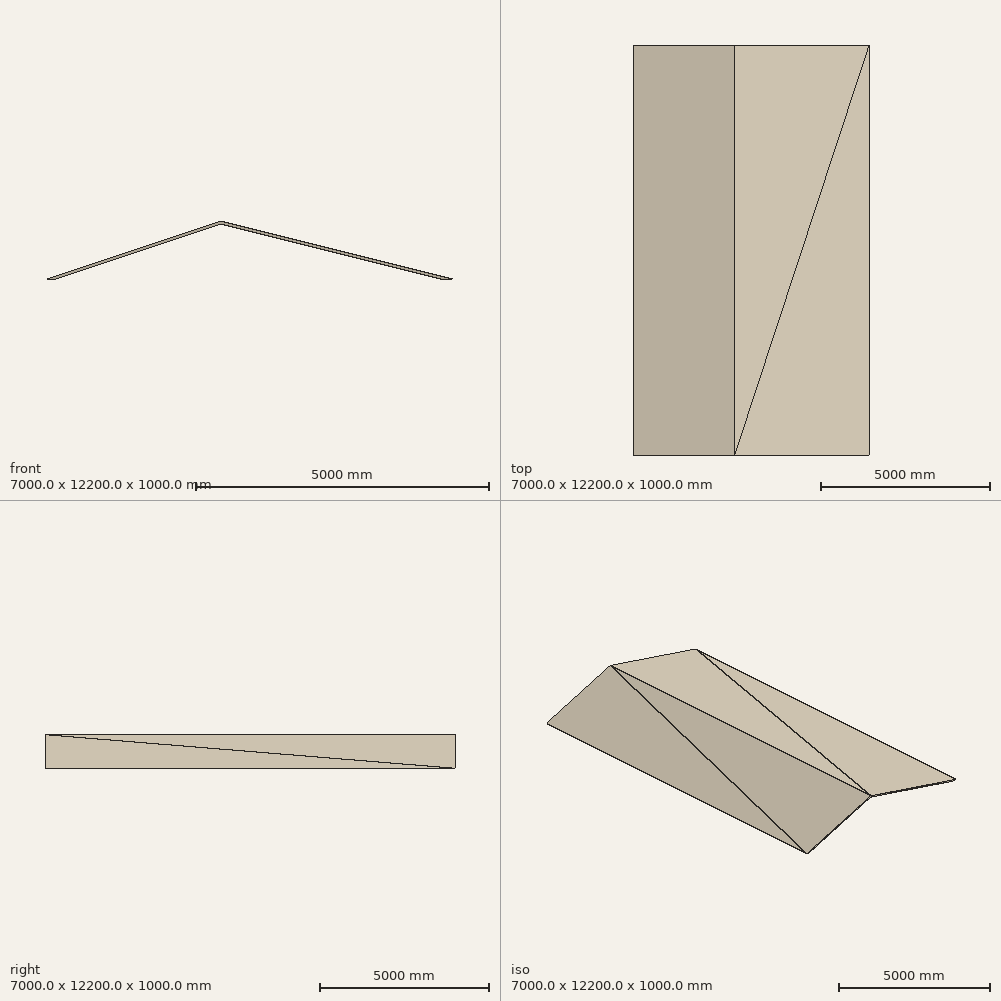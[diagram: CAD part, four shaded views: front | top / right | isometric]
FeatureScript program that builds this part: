
annotation { "Feature Type Name" : "Feature", "Feature Type Description" : "" }
export const myFeature = defineFeature(function(context is Context, id is Id, definition is map)
    precondition{}
    {
        {
            var Q0;
            Q0=qCreatedBy(makeId("Front.planeOp"),FACE);
            var sketch = newSketch(context, id + "F0", { "sketchPlane" : qUnion([Q0])});
            skLineSegment(sketch, "E0", {"start": v(0, 0) * mm, "end": v(7000, 0) * mm, "construction": true});
            skLineSegment(sketch, "E1", {"start": v(0, 0) * mm, "end": v(3000, 1000) * mm});
            skLineSegment(sketch, "E2", {"start": v(3000, 1000) * mm, "end": v(7000, 0) * mm});
            skLineSegment(sketch, "E3", {"start": v(0, 0) * mm, "end": v(154.62, 0) * mm});
            skLineSegment(sketch, "E4", {"start": v(154.62, 0) * mm, "end": v(3000, 948.46) * mm});
            skLineSegment(sketch, "E5", {"start": v(3000, 948.46) * mm, "end": v(6793.84, 0) * mm});
            skLineSegment(sketch, "E6", {"start": v(6793.84, 0) * mm, "end": v(7000, 0) * mm});
            skSolve(sketch);
        }
        {
            var Q0;
            Q0 = qSketchRegion(id + "F0", true);
            extrude(context, id + "F1", {"entities" : qUnion([Q0]), "depth" : 12200 * mm, "offsetDistance" : 25 * mm});
        }
    });
